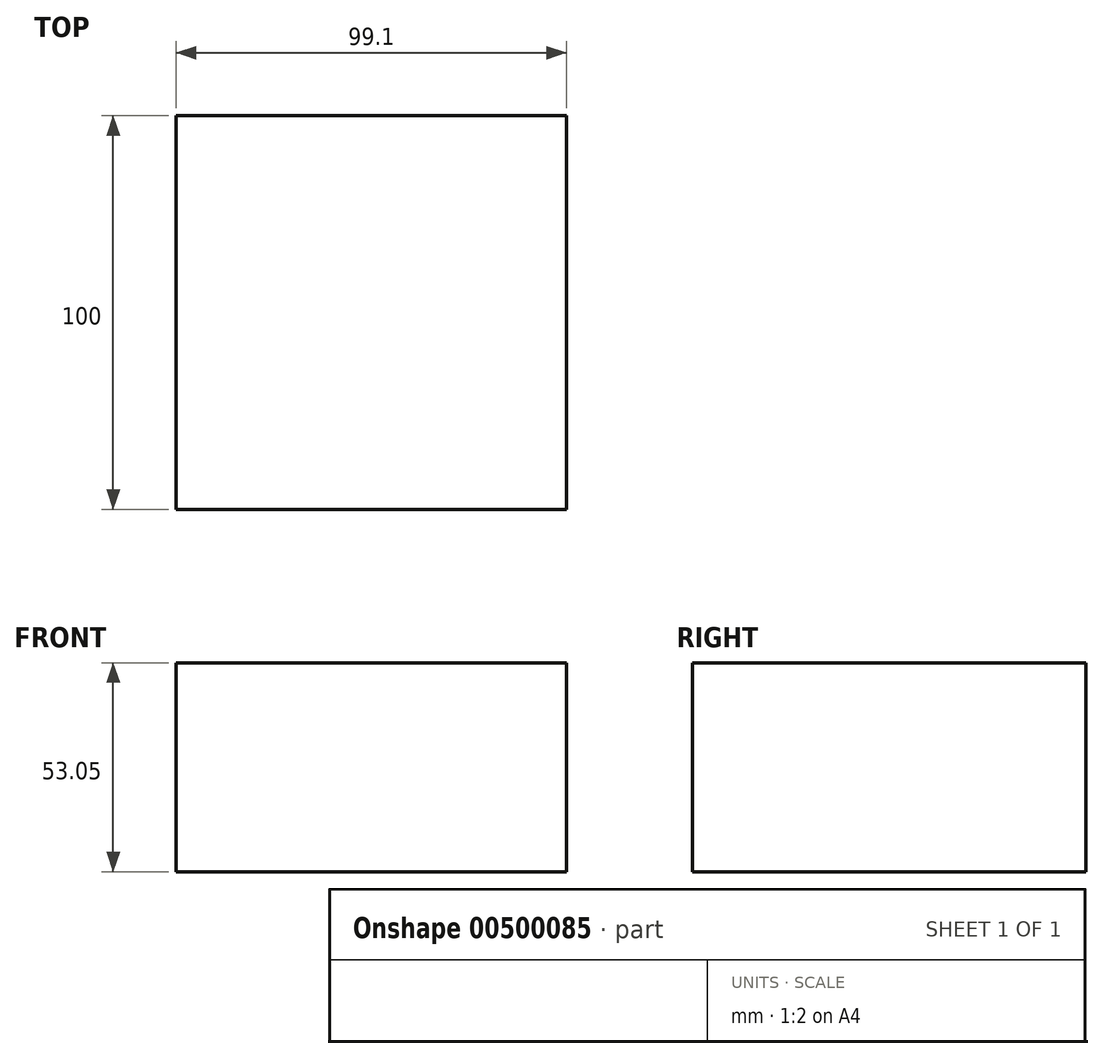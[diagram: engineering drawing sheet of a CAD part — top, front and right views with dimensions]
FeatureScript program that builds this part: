
annotation { "Feature Type Name" : "Feature", "Feature Type Description" : "" }
export const myFeature = defineFeature(function(context is Context, id is Id, definition is map)
    precondition{}
    {
        {
            var Q0;
            Q0=qCreatedBy(makeId("Front.planeOp"),FACE);
            var sketch = newSketch(context, id + "F0", { "sketchPlane" : qUnion([Q0])});
            skLineSegment(sketch, "E0.bottom", {"start": v(-48.1, 24.92) * mm, "end": v(51, 24.92) * mm});
            skLineSegment(sketch, "E0.top", {"start": v(-48.1, -28.13) * mm, "end": v(51, -28.13) * mm});
            skLineSegment(sketch, "E0.left", {"start": v(-48.1, 24.92) * mm, "end": v(-48.1, -28.13) * mm});
            skLineSegment(sketch, "E0.right", {"start": v(51, 24.92) * mm, "end": v(51, -28.13) * mm});
            skSolve(sketch);
        }
        {
            var Q0;
            Q0=makeQuery(id+"F0.imprint","IMPRINT",FACE,{"disambiguationData":[TD([[makeQuery(id+"F0.imprint","IMPRINT",EDGE,{"derivedFrom":sQuery(id+"F0.wireOp",EDGE,"E0.bottom")}),-1.0]])]});
            extrude(context, id + "F1", {"entities" : qUnion([Q0]), "endBound" : BoundingType.SYMMETRIC, "depth" : 100 * mm});
        }
    });
